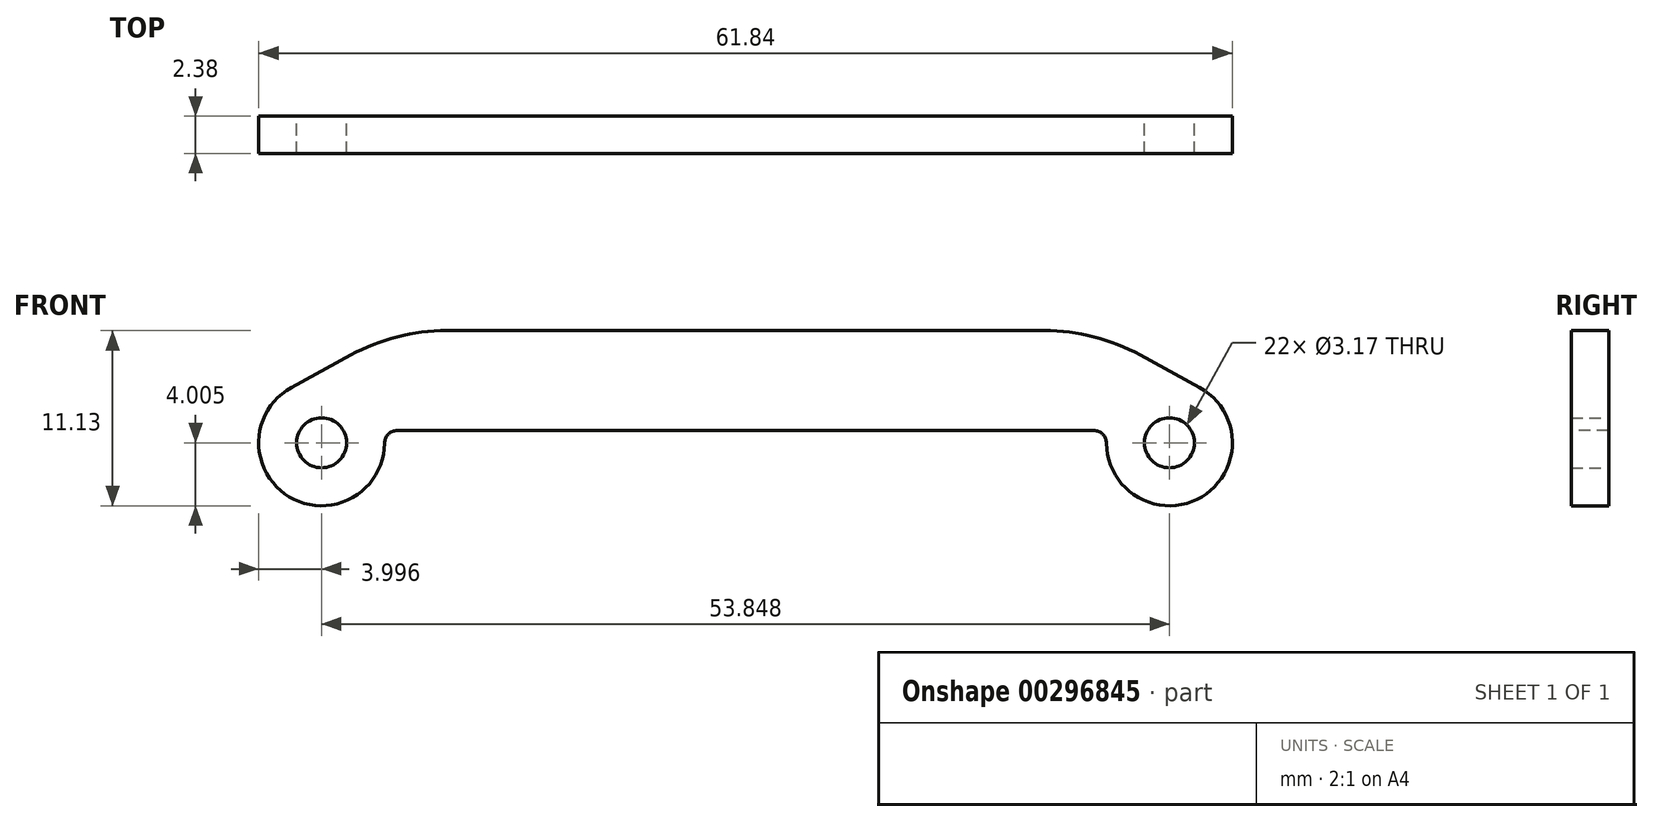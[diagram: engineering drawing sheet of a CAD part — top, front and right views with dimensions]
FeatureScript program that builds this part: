
annotation { "Feature Type Name" : "Feature", "Feature Type Description" : "" }
export const myFeature = defineFeature(function(context is Context, id is Id, definition is map)
    precondition{}
    {
        {
            var Q0;
            Q0=qCreatedBy(makeId("Front.planeOp"),FACE);
            var sketch = newSketch(context, id + "F0", { "sketchPlane" : qUnion([Q0])});
            skLineSegment(sketch, "E0", {"start": v(0, 34.14) * mm, "end": v(0, -36.55) * mm, "construction": true});
            skLineSegment(sketch, "E1", {"start": v(-22.23, 0) * mm, "end": v(22.23, 0) * mm});
            skLineSegment(sketch, "E2", {"start": v(-22.23, 0) * mm, "end": v(-28.84, -3.61) * mm});
            skArc(sketch, "E3", {"start": v(-28.84, -3.61) * mm, "mid": v(-28.97, -10.56) * mm, "end": v(-22.92, -7.13) * mm});
            skLineSegment(sketch, "E4", {"start": v(-22.92, -7.13) * mm, "end": v(-22.92, -6.35) * mm});
            skLineSegment(sketch, "E5", {"start": v(-22.92, -6.35) * mm, "end": v(22.92, -6.35) * mm});
            skPoint(sketch, "E6", {"position": v(-26.92, -11.13) * mm});
            skCircle(sketch, "E7", {"center": v(-26.92, -7.12) * mm, "radius": 1.59 * mm});
            skLineSegment(sketch, "E8.MirrorCS", {"start": v(22.23, 0) * mm, "end": v(28.84, -3.61) * mm});
            skLineSegment(sketch, "E9.MirrorCS", {"start": v(22.92, -7.13) * mm, "end": v(22.92, -6.35) * mm});
            skCircle(sketch, "E10.MirrorC", {"center": v(26.92, -7.12) * mm, "radius": 1.59 * mm});
            skArc(sketch, "E11.MirrorCS", {"start": v(28.84, -3.61) * mm, "mid": v(28.97, -10.56) * mm, "end": v(22.92, -7.13) * mm});
            skSolve(sketch);
        }
        {
            var Q0;
            Q0=makeQuery(id+"F0.imprint","IMPRINT",FACE,{"disambiguationData":[TD([[makeQuery(id+"F0.imprint","IMPRINT",EDGE,{"derivedFrom":sQuery(id+"F0.wireOp",EDGE,"E1")}),-1.0]])]});
            extrude(context, id + "F1", {"entities" : qUnion([Q0]), "endBound" : BoundingType.SYMMETRIC, "depth" : 2.38 * mm});
        }
        {
            var Q0;
            Q0=makeQuery(id+"F1.opExtrude","SWEPT_EDGE",EDGE,{"disambiguationData":[OSD([sQuery(id+"F0.wireOp",EDGE,"E1"),sQuery(id+"F0.wireOp",EDGE,"E8.MirrorCS")])]});
            var Q1;
            Q1=makeQuery(id+"F1.opExtrude","SWEPT_EDGE",EDGE,{"disambiguationData":[OSD([sQuery(id+"F0.wireOp",EDGE,"E1"),sQuery(id+"F0.wireOp",EDGE,"E2")])]});
            fillet(context, id + "F2", {"entities" : qUnion([Q0, Q1]), "radius" : 12.7 * mm, "tangentPropagation" : true, "allowEdgeOverflow" : false});
        }
        {
            var Q0;
            Q0=makeQuery(id+"F1.opExtrude","SWEPT_EDGE",EDGE,{"disambiguationData":[OSD([sQuery(id+"F0.wireOp",EDGE,"E4"),sQuery(id+"F0.wireOp",EDGE,"E5")])]});
            var Q1;
            Q1=makeQuery(id+"F1.opExtrude","SWEPT_EDGE",EDGE,{"disambiguationData":[OSD([sQuery(id+"F0.wireOp",EDGE,"E5"),sQuery(id+"F0.wireOp",EDGE,"E9.MirrorCS")])]});
            fillet(context, id + "F3", {"entities" : qUnion([Q0, Q1]), "radius" : 0.81 * mm, "tangentPropagation" : true, "allowEdgeOverflow" : false});
        }
    });
